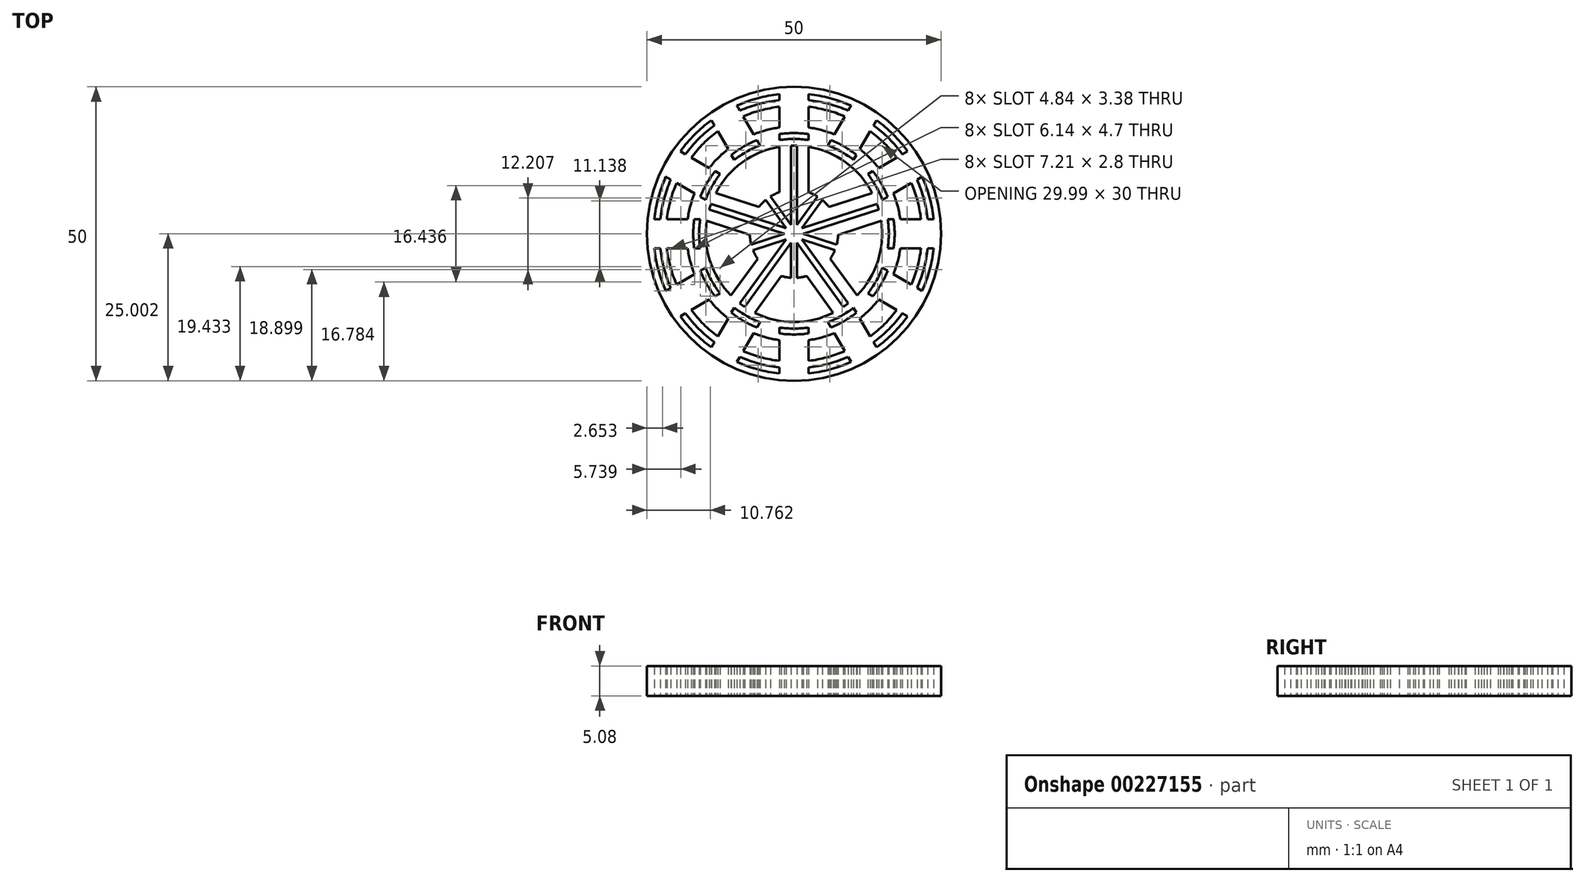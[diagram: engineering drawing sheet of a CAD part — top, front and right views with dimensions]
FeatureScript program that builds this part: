
annotation { "Feature Type Name" : "Feature", "Feature Type Description" : "" }
export const myFeature = defineFeature(function(context is Context, id is Id, definition is map)
    precondition{}
    {
        {
            var Q0;
            Q0=qCreatedBy(makeId("Top.planeOp"),FACE);
            var sketch = newSketch(context, id + "F0", { "sketchPlane" : qUnion([Q0])});
            skCircle(sketch, "E0", {"center": v(-126.34, 15.65) * mm, "radius": 25 * mm});
            skCircle(sketch, "E1", {"center": v(-126.34, 15.65) * mm, "radius": 15 * mm});
            skCircle(sketch, "E2", {"center": v(-126.34, 15.65) * mm, "radius": 18.25 * mm});
            skCircle(sketch, "E3", {"center": v(-126.34, 15.65) * mm, "radius": 21.75 * mm});
            skLineSegment(sketch, "E4", {"start": v(-126.34, 40.65) * mm, "end": v(-126.34, -9.35) * mm});
            skLineSegment(sketch, "E5", {"start": v(-128.84, 33.73) * mm, "end": v(-128.84, 37.26) * mm});
            skLineSegment(sketch, "E6.MirrorCS", {"start": v(-123.84, 33.73) * mm, "end": v(-123.84, 37.26) * mm});
            skLineSegment(sketch, "E7.1.0", {"start": v(-133.22, 32.56) * mm, "end": v(-134.98, 35.61) * mm});
            skLineSegment(sketch, "E7.1.1", {"start": v(-137.55, 30.06) * mm, "end": v(-139.31, 33.11) * mm});
            skLineSegment(sketch, "E7.2.0", {"start": v(-140.75, 26.86) * mm, "end": v(-143.8, 28.62) * mm});
            skLineSegment(sketch, "E7.2.1", {"start": v(-143.25, 22.53) * mm, "end": v(-146.3, 24.3) * mm});
            skLineSegment(sketch, "E7.3.0", {"start": v(-144.42, 18.15) * mm, "end": v(-147.95, 18.15) * mm});
            skLineSegment(sketch, "E7.3.1", {"start": v(-144.42, 13.15) * mm, "end": v(-147.95, 13.15) * mm});
            skLineSegment(sketch, "E7.4.0", {"start": v(-143.25, 8.78) * mm, "end": v(-146.3, 7.01) * mm});
            skLineSegment(sketch, "E7.4.1", {"start": v(-140.75, 4.45) * mm, "end": v(-143.8, 2.68) * mm});
            skLineSegment(sketch, "E7.5.0", {"start": v(-137.55, 1.25) * mm, "end": v(-139.31, -1.8) * mm});
            skLineSegment(sketch, "E7.5.1", {"start": v(-133.22, -1.25) * mm, "end": v(-134.98, -4.3) * mm});
            skLineSegment(sketch, "E7.6.0", {"start": v(-128.84, -2.43) * mm, "end": v(-128.84, -5.95) * mm});
            skLineSegment(sketch, "E7.6.1", {"start": v(-123.84, -2.43) * mm, "end": v(-123.84, -5.95) * mm});
            skLineSegment(sketch, "E7.7.0", {"start": v(-119.47, -1.25) * mm, "end": v(-117.7, -4.3) * mm});
            skLineSegment(sketch, "E7.7.1", {"start": v(-115.14, 1.25) * mm, "end": v(-113.38, -1.8) * mm});
            skLineSegment(sketch, "E7.8.0", {"start": v(-111.94, 4.45) * mm, "end": v(-108.88, 2.68) * mm});
            skLineSegment(sketch, "E7.8.1", {"start": v(-109.44, 8.78) * mm, "end": v(-106.38, 7.01) * mm});
            skLineSegment(sketch, "E7.9.0", {"start": v(-108.27, 13.15) * mm, "end": v(-104.74, 13.15) * mm});
            skLineSegment(sketch, "E7.9.1", {"start": v(-108.27, 18.15) * mm, "end": v(-104.74, 18.15) * mm});
            skLineSegment(sketch, "E7.10.0", {"start": v(-109.44, 22.53) * mm, "end": v(-106.38, 24.3) * mm});
            skLineSegment(sketch, "E7.10.1", {"start": v(-111.94, 26.86) * mm, "end": v(-108.88, 28.62) * mm});
            skLineSegment(sketch, "E7.11.0", {"start": v(-115.14, 30.06) * mm, "end": v(-113.38, 33.11) * mm});
            skLineSegment(sketch, "E7.11.1", {"start": v(-119.47, 32.56) * mm, "end": v(-117.7, 35.61) * mm});
            skLineSegment(sketch, "E8", {"start": v(-128.84, 33.73) * mm, "end": v(-128.84, 30.44) * mm});
            skLineSegment(sketch, "E9", {"start": v(-133.22, 32.56) * mm, "end": v(-131.57, 29.71) * mm});
            skLineSegment(sketch, "E10.1.0", {"start": v(-140.75, 26.86) * mm, "end": v(-137.9, 25.21) * mm});
            skLineSegment(sketch, "E10.1.1", {"start": v(-137.55, 30.06) * mm, "end": v(-135.9, 27.21) * mm});
            skLineSegment(sketch, "E10.2.0", {"start": v(-144.42, 18.15) * mm, "end": v(-141.13, 18.15) * mm});
            skLineSegment(sketch, "E10.2.1", {"start": v(-143.25, 22.53) * mm, "end": v(-140.4, 20.88) * mm});
            skLineSegment(sketch, "E10.3.0", {"start": v(-143.25, 8.78) * mm, "end": v(-140.4, 10.42) * mm});
            skLineSegment(sketch, "E10.3.1", {"start": v(-144.42, 13.15) * mm, "end": v(-141.13, 13.15) * mm});
            skLineSegment(sketch, "E10.4.0", {"start": v(-137.55, 1.25) * mm, "end": v(-135.9, 4.1) * mm});
            skLineSegment(sketch, "E10.4.1", {"start": v(-140.75, 4.45) * mm, "end": v(-137.9, 6.1) * mm});
            skLineSegment(sketch, "E10.5.0", {"start": v(-128.84, -2.43) * mm, "end": v(-128.84, 0.86) * mm});
            skLineSegment(sketch, "E10.5.1", {"start": v(-133.22, -1.25) * mm, "end": v(-131.57, 1.6) * mm});
            skLineSegment(sketch, "E10.6.0", {"start": v(-119.47, -1.25) * mm, "end": v(-121.11, 1.6) * mm});
            skLineSegment(sketch, "E10.6.1", {"start": v(-123.84, -2.43) * mm, "end": v(-123.84, 0.86) * mm});
            skLineSegment(sketch, "E10.7.0", {"start": v(-111.94, 4.45) * mm, "end": v(-114.79, 6.1) * mm});
            skLineSegment(sketch, "E10.7.1", {"start": v(-115.14, 1.25) * mm, "end": v(-116.78, 4.1) * mm});
            skLineSegment(sketch, "E10.8.0", {"start": v(-108.27, 13.15) * mm, "end": v(-111.55, 13.15) * mm});
            skLineSegment(sketch, "E10.8.1", {"start": v(-109.44, 8.78) * mm, "end": v(-112.29, 10.42) * mm});
            skLineSegment(sketch, "E10.9.0", {"start": v(-109.44, 22.53) * mm, "end": v(-112.29, 20.88) * mm});
            skLineSegment(sketch, "E10.9.1", {"start": v(-108.27, 18.15) * mm, "end": v(-111.55, 18.15) * mm});
            skLineSegment(sketch, "E10.10.0", {"start": v(-115.14, 30.06) * mm, "end": v(-116.78, 27.21) * mm});
            skLineSegment(sketch, "E10.10.1", {"start": v(-111.94, 26.86) * mm, "end": v(-114.79, 25.21) * mm});
            skLineSegment(sketch, "E10.11.0", {"start": v(-123.84, 33.73) * mm, "end": v(-123.84, 30.44) * mm});
            skLineSegment(sketch, "E10.11.1", {"start": v(-119.47, 32.56) * mm, "end": v(-121.11, 29.71) * mm});
            skCircle(sketch, "E11", {"center": v(-126.34, 15.65) * mm, "radius": 7.5 * mm});
            skLineSegment(sketch, "E12", {"start": v(-128.84, 30.44) * mm, "end": v(-128.84, 22.72) * mm});
            skLineSegment(sketch, "E13", {"start": v(-123.84, 30.44) * mm, "end": v(-123.84, 22.72) * mm});
            skLineSegment(sketch, "E14.1.0", {"start": v(-139.64, 22.6) * mm, "end": v(-132.3, 20.21) * mm});
            skLineSegment(sketch, "E14.1.1", {"start": v(-141.18, 17.85) * mm, "end": v(-133.84, 15.46) * mm});
            skLineSegment(sketch, "E14.2.0", {"start": v(-137.06, 5.16) * mm, "end": v(-132.52, 11.4) * mm});
            skLineSegment(sketch, "E14.2.1", {"start": v(-133.02, 2.22) * mm, "end": v(-128.48, 8.46) * mm});
            skLineSegment(sketch, "E14.3.0", {"start": v(-119.67, 2.22) * mm, "end": v(-124.21, 8.46) * mm});
            skLineSegment(sketch, "E14.3.1", {"start": v(-115.63, 5.16) * mm, "end": v(-120.17, 11.4) * mm});
            skLineSegment(sketch, "E14.4.0", {"start": v(-111.5, 17.85) * mm, "end": v(-118.85, 15.46) * mm});
            skLineSegment(sketch, "E14.4.1", {"start": v(-113.05, 22.6) * mm, "end": v(-120.4, 20.21) * mm});
            skLineSegment(sketch, "E15", {"start": v(-126.84, 23.14) * mm, "end": v(-126.84, 30.64) * mm});
            skLineSegment(sketch, "E16.MirrorCS", {"start": v(-125.84, 23.14) * mm, "end": v(-125.84, 30.64) * mm});
            skLineSegment(sketch, "E17", {"start": v(-126.84, 23.14) * mm, "end": v(-126.84, 8.17) * mm});
            skLineSegment(sketch, "E18", {"start": v(-125.84, 23.14) * mm, "end": v(-125.84, 8.17) * mm});
            skLineSegment(sketch, "E19.1.0", {"start": v(-133.3, 18.44) * mm, "end": v(-140.45, 20.76) * mm});
            skLineSegment(sketch, "E19.1.1", {"start": v(-133.62, 17.49) * mm, "end": v(-140.76, 19.8) * mm});
            skLineSegment(sketch, "E19.1.2", {"start": v(-133.3, 18.44) * mm, "end": v(-119.07, 13.82) * mm});
            skLineSegment(sketch, "E19.1.3", {"start": v(-133.62, 17.49) * mm, "end": v(-119.38, 12.86) * mm});
            skLineSegment(sketch, "E19.2.0", {"start": v(-131.15, 9.9) * mm, "end": v(-135.56, 3.82) * mm});
            skLineSegment(sketch, "E19.2.1", {"start": v(-130.34, 9.3) * mm, "end": v(-134.75, 3.23) * mm});
            skLineSegment(sketch, "E19.2.2", {"start": v(-131.15, 9.9) * mm, "end": v(-122.35, 22) * mm});
            skLineSegment(sketch, "E19.2.3", {"start": v(-130.34, 9.3) * mm, "end": v(-121.54, 21.41) * mm});
            skLineSegment(sketch, "E19.3.0", {"start": v(-122.35, 9.3) * mm, "end": v(-117.94, 3.23) * mm});
            skLineSegment(sketch, "E19.3.1", {"start": v(-121.54, 9.9) * mm, "end": v(-117.13, 3.82) * mm});
            skLineSegment(sketch, "E19.3.2", {"start": v(-122.35, 9.3) * mm, "end": v(-131.15, 21.41) * mm});
            skLineSegment(sketch, "E19.3.3", {"start": v(-121.54, 9.9) * mm, "end": v(-130.34, 22) * mm});
            skLineSegment(sketch, "E19.4.0", {"start": v(-119.07, 17.49) * mm, "end": v(-111.93, 19.8) * mm});
            skLineSegment(sketch, "E19.4.1", {"start": v(-119.38, 18.44) * mm, "end": v(-112.24, 20.76) * mm});
            skLineSegment(sketch, "E19.4.2", {"start": v(-119.07, 17.49) * mm, "end": v(-133.3, 12.86) * mm});
            skLineSegment(sketch, "E19.4.3", {"start": v(-119.38, 18.44) * mm, "end": v(-133.62, 13.82) * mm});
            skCircle(sketch, "E20", {"center": v(-126.34, 15.65) * mm, "radius": 23.88 * mm});
            skCircle(sketch, "E21", {"center": v(-126.34, 15.65) * mm, "radius": 22.88 * mm});
            skCircle(sketch, "E22", {"center": v(-126.34, 15.65) * mm, "radius": 17.12 * mm});
            skCircle(sketch, "E23", {"center": v(-126.34, 15.65) * mm, "radius": 16.12 * mm});
            skLineSegment(sketch, "E24", {"start": v(-128.84, 38.4) * mm, "end": v(-128.84, 39.4) * mm});
            skLineSegment(sketch, "E25", {"start": v(-123.84, 38.4) * mm, "end": v(-123.84, 39.4) * mm});
            skLineSegment(sketch, "E26.1.0", {"start": v(-135.55, 36.6) * mm, "end": v(-136.05, 37.46) * mm});
            skLineSegment(sketch, "E26.1.1", {"start": v(-139.88, 34.1) * mm, "end": v(-140.38, 34.96) * mm});
            skLineSegment(sketch, "E26.2.0", {"start": v(-144.79, 29.19) * mm, "end": v(-145.66, 29.69) * mm});
            skLineSegment(sketch, "E26.2.1", {"start": v(-147.29, 24.86) * mm, "end": v(-148.16, 25.36) * mm});
            skLineSegment(sketch, "E26.3.0", {"start": v(-149.08, 18.15) * mm, "end": v(-150.09, 18.15) * mm});
            skLineSegment(sketch, "E26.3.1", {"start": v(-149.08, 13.15) * mm, "end": v(-150.09, 13.15) * mm});
            skLineSegment(sketch, "E26.4.0", {"start": v(-147.29, 6.45) * mm, "end": v(-148.16, 5.95) * mm});
            skLineSegment(sketch, "E26.4.1", {"start": v(-144.79, 2.12) * mm, "end": v(-145.66, 1.62) * mm});
            skLineSegment(sketch, "E26.5.0", {"start": v(-139.88, -2.79) * mm, "end": v(-140.38, -3.66) * mm});
            skLineSegment(sketch, "E26.5.1", {"start": v(-135.55, -5.29) * mm, "end": v(-136.05, -6.16) * mm});
            skLineSegment(sketch, "E26.6.0", {"start": v(-128.84, -7.09) * mm, "end": v(-128.84, -8.1) * mm});
            skLineSegment(sketch, "E26.6.1", {"start": v(-123.84, -7.09) * mm, "end": v(-123.84, -8.1) * mm});
            skLineSegment(sketch, "E26.7.0", {"start": v(-117.14, -5.29) * mm, "end": v(-116.64, -6.16) * mm});
            skLineSegment(sketch, "E26.7.1", {"start": v(-112.81, -2.79) * mm, "end": v(-112.3, -3.66) * mm});
            skLineSegment(sketch, "E26.8.0", {"start": v(-107.9, 2.12) * mm, "end": v(-107.03, 1.62) * mm});
            skLineSegment(sketch, "E26.8.1", {"start": v(-105.4, 6.45) * mm, "end": v(-104.53, 5.95) * mm});
            skLineSegment(sketch, "E26.9.0", {"start": v(-103.6, 13.15) * mm, "end": v(-102.6, 13.15) * mm});
            skLineSegment(sketch, "E26.9.1", {"start": v(-103.6, 18.15) * mm, "end": v(-102.6, 18.15) * mm});
            skLineSegment(sketch, "E26.10.0", {"start": v(-105.4, 24.86) * mm, "end": v(-104.53, 25.36) * mm});
            skLineSegment(sketch, "E26.10.1", {"start": v(-107.9, 29.19) * mm, "end": v(-107.03, 29.69) * mm});
            skLineSegment(sketch, "E26.11.0", {"start": v(-112.81, 34.1) * mm, "end": v(-112.3, 34.96) * mm});
            skLineSegment(sketch, "E26.11.1", {"start": v(-117.14, 36.6) * mm, "end": v(-116.64, 37.46) * mm});
            skSolve(sketch);
        }
        {
            var Q0;
            {var subQ0=sQuery(id+"F0.wireOp",EDGE,"E10.7.0");var subQ1=sQuery(id+"F0.wireOp",EDGE,"E1");var subQ2=makeQuery(id+"F0.imprint","INTERSECT",VERTEX,{"derivedFrom":[subQ1,subQ0]});Q0=makeQuery(id+"F0.imprint","IMPRINT",FACE,{"disambiguationData":[TD([[makeQuery(id+"F0.imprint","IMPRINT",EDGE,{"disambiguationData":[TD([[subQ2,-1.0]])],"derivedFrom":subQ1}),-1.0]])]});}
            var Q1;
            {var subQ0=sQuery(id+"F0.wireOp",EDGE,"E10.7.0");var subQ5=sQuery(id+"F0.wireOp",EDGE,"E22");var subQ7=makeQuery(id+"F0.imprint","INTERSECT",VERTEX,{"derivedFrom":[subQ0,subQ5]});Q1=makeQuery(id+"F0.imprint","IMPRINT",FACE,{"disambiguationData":[TD([[makeQuery(id+"F0.imprint","IMPRINT",EDGE,{"disambiguationData":[TD([[subQ7,-1.0]])],"derivedFrom":subQ5}),-1.0]])]});}
            var Q2;
            {var subQ0=sQuery(id+"F0.wireOp",EDGE,"E10.5.0");var subQ1=sQuery(id+"F0.wireOp",EDGE,"E1");var subQ2=makeQuery(id+"F0.imprint","INTERSECT",VERTEX,{"derivedFrom":[subQ1,subQ0]});Q2=makeQuery(id+"F0.imprint","IMPRINT",FACE,{"disambiguationData":[TD([[makeQuery(id+"F0.imprint","IMPRINT",EDGE,{"disambiguationData":[TD([[subQ2,-1.0]])],"derivedFrom":subQ1}),-1.0]])]});}
            var Q3;
            {var subQ1=sQuery(id+"F0.wireOp",EDGE,"E2");var subQ3=sQuery(id+"F0.wireOp",EDGE,"E4");var subQ4=makeQuery(id+"F0.imprint","INTERSECT",VERTEX,{"disambiguationData":[OD(1.0)],"derivedFrom":[subQ1,subQ3]});Q3=makeQuery(id+"F0.imprint","IMPRINT",FACE,{"disambiguationData":[TD([[makeQuery(id+"F0.imprint","IMPRINT",EDGE,{"disambiguationData":[TD([[subQ4,1.0]])],"derivedFrom":subQ3}),-1.0]])]});}
            var Q4;
            {var subQ0=sQuery(id+"F0.wireOp",EDGE,"E5");Q4=makeQuery(id+"F0.imprint","IMPRINT",FACE,{"disambiguationData":[TD([[makeQuery(id+"F0.imprint","IMPRINT",EDGE,{"derivedFrom":subQ0}),-1.0]])]});}
            var Q5;
            {var subQ0=sQuery(id+"F0.wireOp",EDGE,"E7.6.0");Q5=makeQuery(id+"F0.imprint","IMPRINT",FACE,{"disambiguationData":[TD([[makeQuery(id+"F0.imprint","IMPRINT",EDGE,{"derivedFrom":subQ0}),1.0]])]});}
            var Q6;
            {var subQ0=sQuery(id+"F0.wireOp",EDGE,"E4");var subQ1=sQuery(id+"F0.wireOp",EDGE,"E0");var subQ2=makeQuery(id+"F0.imprint","INTERSECT",VERTEX,{"disambiguationData":[OD(0.0)],"derivedFrom":[subQ1,subQ0]});Q6=makeQuery(id+"F0.imprint","IMPRINT",FACE,{"disambiguationData":[TD([[makeQuery(id+"F0.imprint","IMPRINT",EDGE,{"disambiguationData":[TD([[subQ2,-1.0]])],"derivedFrom":subQ1}),1.0]])]});}
            var Q7;
            {var subQ0=sQuery(id+"F0.wireOp",EDGE,"E4");var subQ1=sQuery(id+"F0.wireOp",EDGE,"E0");var subQ2=makeQuery(id+"F0.imprint","INTERSECT",VERTEX,{"disambiguationData":[OD(0.0)],"derivedFrom":[subQ1,subQ0]});Q7=makeQuery(id+"F0.imprint","IMPRINT",FACE,{"disambiguationData":[TD([[makeQuery(id+"F0.imprint","IMPRINT",EDGE,{"disambiguationData":[TD([[subQ2,1.0]])],"derivedFrom":subQ1}),1.0]])]});}
            var Q8;
            {var subQ0=sQuery(id+"F0.wireOp",EDGE,"E9");var subQ1=sQuery(id+"F0.wireOp",EDGE,"E1");var subQ2=makeQuery(id+"F0.imprint","INTERSECT",VERTEX,{"derivedFrom":[subQ1,subQ0]});Q8=makeQuery(id+"F0.imprint","IMPRINT",FACE,{"disambiguationData":[TD([[makeQuery(id+"F0.imprint","IMPRINT",EDGE,{"disambiguationData":[TD([[subQ2,-1.0]])],"derivedFrom":subQ1}),-1.0]])]});}
            var Q9;
            {var subQ0=sQuery(id+"F0.wireOp",EDGE,"E9");var subQ5=sQuery(id+"F0.wireOp",EDGE,"E22");var subQ6=makeQuery(id+"F0.imprint","INTERSECT",VERTEX,{"derivedFrom":[subQ0,subQ5]});Q9=makeQuery(id+"F0.imprint","IMPRINT",FACE,{"disambiguationData":[TD([[makeQuery(id+"F0.imprint","IMPRINT",EDGE,{"disambiguationData":[TD([[subQ6,-1.0]])],"derivedFrom":subQ5}),-1.0]])]});}
            var Q10;
            {var subQ0=sQuery(id+"F0.wireOp",EDGE,"E7.1.0");Q10=makeQuery(id+"F0.imprint","IMPRINT",FACE,{"disambiguationData":[TD([[makeQuery(id+"F0.imprint","IMPRINT",EDGE,{"derivedFrom":subQ0}),1.0]])]});}
            var Q11;
            {var subQ0=sQuery(id+"F0.wireOp",EDGE,"E7.2.0");Q11=makeQuery(id+"F0.imprint","IMPRINT",FACE,{"disambiguationData":[TD([[makeQuery(id+"F0.imprint","IMPRINT",EDGE,{"derivedFrom":subQ0}),1.0]])]});}
            var Q12;
            {var subQ0=sQuery(id+"F0.wireOp",EDGE,"E10.1.0");var subQ5=sQuery(id+"F0.wireOp",EDGE,"E22");var subQ6=makeQuery(id+"F0.imprint","INTERSECT",VERTEX,{"derivedFrom":[subQ0,subQ5]});Q12=makeQuery(id+"F0.imprint","IMPRINT",FACE,{"disambiguationData":[TD([[makeQuery(id+"F0.imprint","IMPRINT",EDGE,{"disambiguationData":[TD([[subQ6,-1.0]])],"derivedFrom":subQ5}),-1.0]])]});}
            var Q13;
            {var subQ0=sQuery(id+"F0.wireOp",EDGE,"E7.3.0");Q13=makeQuery(id+"F0.imprint","IMPRINT",FACE,{"disambiguationData":[TD([[makeQuery(id+"F0.imprint","IMPRINT",EDGE,{"derivedFrom":subQ0}),1.0]])]});}
            var Q14;
            {var subQ0=sQuery(id+"F0.wireOp",EDGE,"E10.2.0");var subQ5=sQuery(id+"F0.wireOp",EDGE,"E22");var subQ6=makeQuery(id+"F0.imprint","INTERSECT",VERTEX,{"derivedFrom":[subQ0,subQ5]});Q14=makeQuery(id+"F0.imprint","IMPRINT",FACE,{"disambiguationData":[TD([[makeQuery(id+"F0.imprint","IMPRINT",EDGE,{"disambiguationData":[TD([[subQ6,-1.0]])],"derivedFrom":subQ5}),-1.0]])]});}
            var Q15;
            {var subQ0=sQuery(id+"F0.wireOp",EDGE,"E10.1.0");var subQ1=sQuery(id+"F0.wireOp",EDGE,"E1");var subQ2=makeQuery(id+"F0.imprint","INTERSECT",VERTEX,{"derivedFrom":[subQ1,subQ0]});Q15=makeQuery(id+"F0.imprint","IMPRINT",FACE,{"disambiguationData":[TD([[makeQuery(id+"F0.imprint","IMPRINT",EDGE,{"disambiguationData":[TD([[subQ2,1.0]])],"derivedFrom":subQ1}),-1.0]])]});}
            var Q16;
            {var subQ3=sQuery(id+"F0.wireOp",EDGE,"E10.1.0");var subQ5=sQuery(id+"F0.wireOp",EDGE,"E22");var subQ6=makeQuery(id+"F0.imprint","INTERSECT",VERTEX,{"derivedFrom":[subQ3,subQ5]});Q16=makeQuery(id+"F0.imprint","IMPRINT",FACE,{"disambiguationData":[TD([[makeQuery(id+"F0.imprint","IMPRINT",EDGE,{"disambiguationData":[TD([[subQ6,1.0]])],"derivedFrom":subQ5}),-1.0]])]});}
            var Q17;
            {var subQ3=sQuery(id+"F0.wireOp",EDGE,"E10.2.0");var subQ5=sQuery(id+"F0.wireOp",EDGE,"E22");var subQ6=makeQuery(id+"F0.imprint","INTERSECT",VERTEX,{"derivedFrom":[subQ3,subQ5]});Q17=makeQuery(id+"F0.imprint","IMPRINT",FACE,{"disambiguationData":[TD([[makeQuery(id+"F0.imprint","IMPRINT",EDGE,{"disambiguationData":[TD([[subQ6,1.0]])],"derivedFrom":subQ5}),-1.0]])]});}
            var Q18;
            {var subQ0=sQuery(id+"F0.wireOp",EDGE,"E10.3.0");var subQ1=sQuery(id+"F0.wireOp",EDGE,"E1");var subQ2=makeQuery(id+"F0.imprint","INTERSECT",VERTEX,{"derivedFrom":[subQ1,subQ0]});Q18=makeQuery(id+"F0.imprint","IMPRINT",FACE,{"disambiguationData":[TD([[makeQuery(id+"F0.imprint","IMPRINT",EDGE,{"disambiguationData":[TD([[subQ2,1.0]])],"derivedFrom":subQ1}),-1.0]])]});}
            var Q19;
            {var subQ3=sQuery(id+"F0.wireOp",EDGE,"E10.3.0");var subQ5=sQuery(id+"F0.wireOp",EDGE,"E22");var subQ7=makeQuery(id+"F0.imprint","INTERSECT",VERTEX,{"derivedFrom":[subQ3,subQ5]});Q19=makeQuery(id+"F0.imprint","IMPRINT",FACE,{"disambiguationData":[TD([[makeQuery(id+"F0.imprint","IMPRINT",EDGE,{"disambiguationData":[TD([[subQ7,1.0]])],"derivedFrom":subQ5}),-1.0]])]});}
            var Q20;
            {var subQ0=sQuery(id+"F0.wireOp",EDGE,"E10.3.0");var subQ1=sQuery(id+"F0.wireOp",EDGE,"E1");var subQ2=makeQuery(id+"F0.imprint","INTERSECT",VERTEX,{"derivedFrom":[subQ1,subQ0]});Q20=makeQuery(id+"F0.imprint","IMPRINT",FACE,{"disambiguationData":[TD([[makeQuery(id+"F0.imprint","IMPRINT",EDGE,{"disambiguationData":[TD([[subQ2,-1.0]])],"derivedFrom":subQ1}),-1.0]])]});}
            var Q21;
            {var subQ0=sQuery(id+"F0.wireOp",EDGE,"E10.3.0");var subQ5=sQuery(id+"F0.wireOp",EDGE,"E22");var subQ7=makeQuery(id+"F0.imprint","INTERSECT",VERTEX,{"derivedFrom":[subQ0,subQ5]});Q21=makeQuery(id+"F0.imprint","IMPRINT",FACE,{"disambiguationData":[TD([[makeQuery(id+"F0.imprint","IMPRINT",EDGE,{"disambiguationData":[TD([[subQ7,-1.0]])],"derivedFrom":subQ5}),-1.0]])]});}
            var Q22;
            {var subQ0=sQuery(id+"F0.wireOp",EDGE,"E7.4.0");Q22=makeQuery(id+"F0.imprint","IMPRINT",FACE,{"disambiguationData":[TD([[makeQuery(id+"F0.imprint","IMPRINT",EDGE,{"derivedFrom":subQ0}),1.0]])]});}
            var Q23;
            {var subQ0=sQuery(id+"F0.wireOp",EDGE,"E7.5.0");Q23=makeQuery(id+"F0.imprint","IMPRINT",FACE,{"disambiguationData":[TD([[makeQuery(id+"F0.imprint","IMPRINT",EDGE,{"derivedFrom":subQ0}),1.0]])]});}
            var Q24;
            {var subQ0=sQuery(id+"F0.wireOp",EDGE,"E10.4.0");var subQ5=sQuery(id+"F0.wireOp",EDGE,"E22");var subQ6=makeQuery(id+"F0.imprint","INTERSECT",VERTEX,{"derivedFrom":[subQ0,subQ5]});Q24=makeQuery(id+"F0.imprint","IMPRINT",FACE,{"disambiguationData":[TD([[makeQuery(id+"F0.imprint","IMPRINT",EDGE,{"disambiguationData":[TD([[subQ6,-1.0]])],"derivedFrom":subQ5}),-1.0]])]});}
            var Q25;
            {var subQ3=sQuery(id+"F0.wireOp",EDGE,"E10.4.0");var subQ5=sQuery(id+"F0.wireOp",EDGE,"E22");var subQ6=makeQuery(id+"F0.imprint","INTERSECT",VERTEX,{"derivedFrom":[subQ3,subQ5]});Q25=makeQuery(id+"F0.imprint","IMPRINT",FACE,{"disambiguationData":[TD([[makeQuery(id+"F0.imprint","IMPRINT",EDGE,{"disambiguationData":[TD([[subQ6,1.0]])],"derivedFrom":subQ5}),-1.0]])]});}
            var Q26;
            {var subQ0=sQuery(id+"F0.wireOp",EDGE,"E10.5.0");var subQ1=sQuery(id+"F0.wireOp",EDGE,"E1");var subQ2=makeQuery(id+"F0.imprint","INTERSECT",VERTEX,{"derivedFrom":[subQ1,subQ0]});Q26=makeQuery(id+"F0.imprint","IMPRINT",FACE,{"disambiguationData":[TD([[makeQuery(id+"F0.imprint","IMPRINT",EDGE,{"disambiguationData":[TD([[subQ2,1.0]])],"derivedFrom":subQ1}),-1.0]])]});}
            var Q27;
            {var subQ3=sQuery(id+"F0.wireOp",EDGE,"E10.5.0");var subQ5=sQuery(id+"F0.wireOp",EDGE,"E22");var subQ6=makeQuery(id+"F0.imprint","INTERSECT",VERTEX,{"derivedFrom":[subQ3,subQ5]});Q27=makeQuery(id+"F0.imprint","IMPRINT",FACE,{"disambiguationData":[TD([[makeQuery(id+"F0.imprint","IMPRINT",EDGE,{"disambiguationData":[TD([[subQ6,1.0]])],"derivedFrom":subQ5}),-1.0]])]});}
            var Q28;
            {var subQ0=sQuery(id+"F0.wireOp",EDGE,"E10.6.1");var subQ1=sQuery(id+"F0.wireOp",EDGE,"E1");var subQ2=makeQuery(id+"F0.imprint","INTERSECT",VERTEX,{"derivedFrom":[subQ1,subQ0]});Q28=makeQuery(id+"F0.imprint","IMPRINT",FACE,{"disambiguationData":[TD([[makeQuery(id+"F0.imprint","IMPRINT",EDGE,{"disambiguationData":[TD([[subQ2,1.0]])],"derivedFrom":subQ1}),-1.0]])]});}
            var Q29;
            {var subQ1=sQuery(id+"F0.wireOp",EDGE,"E2");var subQ3=sQuery(id+"F0.wireOp",EDGE,"E4");var subQ4=makeQuery(id+"F0.imprint","INTERSECT",VERTEX,{"disambiguationData":[OD(1.0)],"derivedFrom":[subQ1,subQ3]});Q29=makeQuery(id+"F0.imprint","IMPRINT",FACE,{"disambiguationData":[TD([[makeQuery(id+"F0.imprint","IMPRINT",EDGE,{"disambiguationData":[TD([[subQ4,1.0]])],"derivedFrom":subQ3}),1.0]])]});}
            var Q30;
            {var subQ0=sQuery(id+"F0.wireOp",EDGE,"E7.6.1");Q30=makeQuery(id+"F0.imprint","IMPRINT",FACE,{"disambiguationData":[TD([[makeQuery(id+"F0.imprint","IMPRINT",EDGE,{"derivedFrom":subQ0}),-1.0]])]});}
            var Q31;
            {var subQ0=sQuery(id+"F0.wireOp",EDGE,"E10.6.0");var subQ1=sQuery(id+"F0.wireOp",EDGE,"E1");var subQ2=makeQuery(id+"F0.imprint","INTERSECT",VERTEX,{"derivedFrom":[subQ1,subQ0]});Q31=makeQuery(id+"F0.imprint","IMPRINT",FACE,{"disambiguationData":[TD([[makeQuery(id+"F0.imprint","IMPRINT",EDGE,{"disambiguationData":[TD([[subQ2,1.0]])],"derivedFrom":subQ1}),-1.0]])]});}
            var Q32;
            {var subQ3=sQuery(id+"F0.wireOp",EDGE,"E10.6.0");var subQ5=sQuery(id+"F0.wireOp",EDGE,"E22");var subQ6=makeQuery(id+"F0.imprint","INTERSECT",VERTEX,{"derivedFrom":[subQ3,subQ5]});Q32=makeQuery(id+"F0.imprint","IMPRINT",FACE,{"disambiguationData":[TD([[makeQuery(id+"F0.imprint","IMPRINT",EDGE,{"disambiguationData":[TD([[subQ6,1.0]])],"derivedFrom":subQ5}),-1.0]])]});}
            var Q33;
            {var subQ0=sQuery(id+"F0.wireOp",EDGE,"E10.6.0");var subQ5=sQuery(id+"F0.wireOp",EDGE,"E22");var subQ6=makeQuery(id+"F0.imprint","INTERSECT",VERTEX,{"derivedFrom":[subQ0,subQ5]});Q33=makeQuery(id+"F0.imprint","IMPRINT",FACE,{"disambiguationData":[TD([[makeQuery(id+"F0.imprint","IMPRINT",EDGE,{"disambiguationData":[TD([[subQ6,-1.0]])],"derivedFrom":subQ5}),-1.0]])]});}
            var Q34;
            {var subQ3=sQuery(id+"F0.wireOp",EDGE,"E10.7.0");var subQ5=sQuery(id+"F0.wireOp",EDGE,"E22");var subQ7=makeQuery(id+"F0.imprint","INTERSECT",VERTEX,{"derivedFrom":[subQ3,subQ5]});Q34=makeQuery(id+"F0.imprint","IMPRINT",FACE,{"disambiguationData":[TD([[makeQuery(id+"F0.imprint","IMPRINT",EDGE,{"disambiguationData":[TD([[subQ7,1.0]])],"derivedFrom":subQ5}),-1.0]])]});}
            var Q35;
            {var subQ0=sQuery(id+"F0.wireOp",EDGE,"E10.8.0");var subQ1=sQuery(id+"F0.wireOp",EDGE,"E1");var subQ2=makeQuery(id+"F0.imprint","INTERSECT",VERTEX,{"derivedFrom":[subQ1,subQ0]});Q35=makeQuery(id+"F0.imprint","IMPRINT",FACE,{"disambiguationData":[TD([[makeQuery(id+"F0.imprint","IMPRINT",EDGE,{"disambiguationData":[TD([[subQ2,1.0]])],"derivedFrom":subQ1}),-1.0]])]});}
            var Q36;
            {var subQ3=sQuery(id+"F0.wireOp",EDGE,"E10.8.0");var subQ5=sQuery(id+"F0.wireOp",EDGE,"E22");var subQ6=makeQuery(id+"F0.imprint","INTERSECT",VERTEX,{"derivedFrom":[subQ3,subQ5]});Q36=makeQuery(id+"F0.imprint","IMPRINT",FACE,{"disambiguationData":[TD([[makeQuery(id+"F0.imprint","IMPRINT",EDGE,{"disambiguationData":[TD([[subQ6,1.0]])],"derivedFrom":subQ5}),-1.0]])]});}
            var Q37;
            {var subQ0=sQuery(id+"F0.wireOp",EDGE,"E10.8.0");var subQ5=sQuery(id+"F0.wireOp",EDGE,"E22");var subQ6=makeQuery(id+"F0.imprint","INTERSECT",VERTEX,{"derivedFrom":[subQ0,subQ5]});Q37=makeQuery(id+"F0.imprint","IMPRINT",FACE,{"disambiguationData":[TD([[makeQuery(id+"F0.imprint","IMPRINT",EDGE,{"disambiguationData":[TD([[subQ6,-1.0]])],"derivedFrom":subQ5}),-1.0]])]});}
            var Q38;
            {var subQ3=sQuery(id+"F0.wireOp",EDGE,"E10.9.0");var subQ5=sQuery(id+"F0.wireOp",EDGE,"E22");var subQ6=makeQuery(id+"F0.imprint","INTERSECT",VERTEX,{"derivedFrom":[subQ3,subQ5]});Q38=makeQuery(id+"F0.imprint","IMPRINT",FACE,{"disambiguationData":[TD([[makeQuery(id+"F0.imprint","IMPRINT",EDGE,{"disambiguationData":[TD([[subQ6,1.0]])],"derivedFrom":subQ5}),-1.0]])]});}
            var Q39;
            {var subQ0=sQuery(id+"F0.wireOp",EDGE,"E10.9.0");var subQ5=sQuery(id+"F0.wireOp",EDGE,"E22");var subQ6=makeQuery(id+"F0.imprint","INTERSECT",VERTEX,{"derivedFrom":[subQ0,subQ5]});Q39=makeQuery(id+"F0.imprint","IMPRINT",FACE,{"disambiguationData":[TD([[makeQuery(id+"F0.imprint","IMPRINT",EDGE,{"disambiguationData":[TD([[subQ6,-1.0]])],"derivedFrom":subQ5}),-1.0]])]});}
            var Q40;
            {var subQ0=sQuery(id+"F0.wireOp",EDGE,"E10.10.0");var subQ1=sQuery(id+"F0.wireOp",EDGE,"E1");var subQ2=makeQuery(id+"F0.imprint","INTERSECT",VERTEX,{"derivedFrom":[subQ1,subQ0]});Q40=makeQuery(id+"F0.imprint","IMPRINT",FACE,{"disambiguationData":[TD([[makeQuery(id+"F0.imprint","IMPRINT",EDGE,{"disambiguationData":[TD([[subQ2,1.0]])],"derivedFrom":subQ1}),-1.0]])]});}
            var Q41;
            {var subQ3=sQuery(id+"F0.wireOp",EDGE,"E10.10.0");var subQ5=sQuery(id+"F0.wireOp",EDGE,"E22");var subQ6=makeQuery(id+"F0.imprint","INTERSECT",VERTEX,{"derivedFrom":[subQ3,subQ5]});Q41=makeQuery(id+"F0.imprint","IMPRINT",FACE,{"disambiguationData":[TD([[makeQuery(id+"F0.imprint","IMPRINT",EDGE,{"disambiguationData":[TD([[subQ6,1.0]])],"derivedFrom":subQ5}),-1.0]])]});}
            var Q42;
            {var subQ0=sQuery(id+"F0.wireOp",EDGE,"E10.10.0");var subQ1=sQuery(id+"F0.wireOp",EDGE,"E1");var subQ2=makeQuery(id+"F0.imprint","INTERSECT",VERTEX,{"derivedFrom":[subQ1,subQ0]});Q42=makeQuery(id+"F0.imprint","IMPRINT",FACE,{"disambiguationData":[TD([[makeQuery(id+"F0.imprint","IMPRINT",EDGE,{"disambiguationData":[TD([[subQ2,-1.0]])],"derivedFrom":subQ1}),-1.0]])]});}
            var Q43;
            {var subQ0=sQuery(id+"F0.wireOp",EDGE,"E10.10.0");var subQ5=sQuery(id+"F0.wireOp",EDGE,"E22");var subQ6=makeQuery(id+"F0.imprint","INTERSECT",VERTEX,{"derivedFrom":[subQ0,subQ5]});Q43=makeQuery(id+"F0.imprint","IMPRINT",FACE,{"disambiguationData":[TD([[makeQuery(id+"F0.imprint","IMPRINT",EDGE,{"disambiguationData":[TD([[subQ6,-1.0]])],"derivedFrom":subQ5}),-1.0]])]});}
            var Q44;
            {var subQ1=sQuery(id+"F0.wireOp",EDGE,"E1");var subQ3=sQuery(id+"F0.wireOp",EDGE,"E10.11.1");var subQ4=makeQuery(id+"F0.imprint","INTERSECT",VERTEX,{"derivedFrom":[subQ1,subQ3]});Q44=makeQuery(id+"F0.imprint","IMPRINT",FACE,{"disambiguationData":[TD([[makeQuery(id+"F0.imprint","IMPRINT",EDGE,{"disambiguationData":[TD([[subQ4,1.0]])],"derivedFrom":subQ3}),-1.0]])]});}
            var Q45;
            {var subQ0=sQuery(id+"F0.wireOp",EDGE,"E10.11.0");var subQ5=sQuery(id+"F0.wireOp",EDGE,"E22");var subQ6=makeQuery(id+"F0.imprint","INTERSECT",VERTEX,{"derivedFrom":[subQ0,subQ5]});Q45=makeQuery(id+"F0.imprint","IMPRINT",FACE,{"disambiguationData":[TD([[makeQuery(id+"F0.imprint","IMPRINT",EDGE,{"disambiguationData":[TD([[subQ6,1.0]])],"derivedFrom":subQ5}),-1.0]])]});}
            var Q46;
            {var subQ1=sQuery(id+"F0.wireOp",EDGE,"E2");var subQ3=sQuery(id+"F0.wireOp",EDGE,"E4");var subQ4=makeQuery(id+"F0.imprint","INTERSECT",VERTEX,{"disambiguationData":[OD(0.0)],"derivedFrom":[subQ1,subQ3]});Q46=makeQuery(id+"F0.imprint","IMPRINT",FACE,{"disambiguationData":[TD([[makeQuery(id+"F0.imprint","IMPRINT",EDGE,{"disambiguationData":[TD([[subQ4,-1.0]])],"derivedFrom":subQ3}),1.0]])]});}
            var Q47;
            {var subQ1=sQuery(id+"F0.wireOp",EDGE,"E2");var subQ3=sQuery(id+"F0.wireOp",EDGE,"E4");var subQ4=makeQuery(id+"F0.imprint","INTERSECT",VERTEX,{"disambiguationData":[OD(0.0)],"derivedFrom":[subQ1,subQ3]});Q47=makeQuery(id+"F0.imprint","IMPRINT",FACE,{"disambiguationData":[TD([[makeQuery(id+"F0.imprint","IMPRINT",EDGE,{"disambiguationData":[TD([[subQ4,-1.0]])],"derivedFrom":subQ3}),-1.0]])]});}
            var Q48;
            {var subQ1=sQuery(id+"F0.wireOp",EDGE,"E1");var subQ3=sQuery(id+"F0.wireOp",EDGE,"E9");var subQ4=makeQuery(id+"F0.imprint","INTERSECT",VERTEX,{"derivedFrom":[subQ1,subQ3]});Q48=makeQuery(id+"F0.imprint","IMPRINT",FACE,{"disambiguationData":[TD([[makeQuery(id+"F0.imprint","IMPRINT",EDGE,{"disambiguationData":[TD([[subQ4,1.0]])],"derivedFrom":subQ3}),1.0]])]});}
            var Q49;
            {var subQ0=sQuery(id+"F0.wireOp",EDGE,"E8");var subQ5=sQuery(id+"F0.wireOp",EDGE,"E22");var subQ6=makeQuery(id+"F0.imprint","INTERSECT",VERTEX,{"derivedFrom":[subQ0,subQ5]});Q49=makeQuery(id+"F0.imprint","IMPRINT",FACE,{"disambiguationData":[TD([[makeQuery(id+"F0.imprint","IMPRINT",EDGE,{"disambiguationData":[TD([[subQ6,-1.0]])],"derivedFrom":subQ5}),-1.0]])]});}
            var Q50;
            {var subQ0=sQuery(id+"F0.wireOp",EDGE,"E6.MirrorCS");Q50=makeQuery(id+"F0.imprint","IMPRINT",FACE,{"disambiguationData":[TD([[makeQuery(id+"F0.imprint","IMPRINT",EDGE,{"derivedFrom":subQ0}),1.0]])]});}
            var Q51;
            {var subQ0=sQuery(id+"F0.wireOp",EDGE,"E7.11.0");Q51=makeQuery(id+"F0.imprint","IMPRINT",FACE,{"disambiguationData":[TD([[makeQuery(id+"F0.imprint","IMPRINT",EDGE,{"derivedFrom":subQ0}),1.0]])]});}
            var Q52;
            {var subQ0=sQuery(id+"F0.wireOp",EDGE,"E7.10.0");Q52=makeQuery(id+"F0.imprint","IMPRINT",FACE,{"disambiguationData":[TD([[makeQuery(id+"F0.imprint","IMPRINT",EDGE,{"derivedFrom":subQ0}),1.0]])]});}
            var Q53;
            {var subQ0=sQuery(id+"F0.wireOp",EDGE,"E7.9.0");Q53=makeQuery(id+"F0.imprint","IMPRINT",FACE,{"disambiguationData":[TD([[makeQuery(id+"F0.imprint","IMPRINT",EDGE,{"derivedFrom":subQ0}),1.0]])]});}
            var Q54;
            {var subQ0=sQuery(id+"F0.wireOp",EDGE,"E7.8.0");Q54=makeQuery(id+"F0.imprint","IMPRINT",FACE,{"disambiguationData":[TD([[makeQuery(id+"F0.imprint","IMPRINT",EDGE,{"derivedFrom":subQ0}),1.0]])]});}
            var Q55;
            {var subQ0=sQuery(id+"F0.wireOp",EDGE,"E7.7.0");Q55=makeQuery(id+"F0.imprint","IMPRINT",FACE,{"disambiguationData":[TD([[makeQuery(id+"F0.imprint","IMPRINT",EDGE,{"derivedFrom":subQ0}),1.0]])]});}
            var Q56;
            {var subQ0=sQuery(id+"F0.wireOp",EDGE,"E14.1.0");Q56=makeQuery(id+"F0.imprint","IMPRINT",FACE,{"disambiguationData":[TD([[makeQuery(id+"F0.imprint","IMPRINT",EDGE,{"derivedFrom":subQ0}),-1.0]])]});}
            var Q57;
            {var subQ0=sQuery(id+"F0.wireOp",EDGE,"E13");Q57=makeQuery(id+"F0.imprint","IMPRINT",FACE,{"disambiguationData":[TD([[makeQuery(id+"F0.imprint","IMPRINT",EDGE,{"derivedFrom":subQ0}),-1.0]])]});}
            var Q58;
            {var subQ0=sQuery(id+"F0.wireOp",EDGE,"E12");Q58=makeQuery(id+"F0.imprint","IMPRINT",FACE,{"disambiguationData":[TD([[makeQuery(id+"F0.imprint","IMPRINT",EDGE,{"derivedFrom":subQ0}),1.0]])]});}
            var Q59;
            {var subQ0=sQuery(id+"F0.wireOp",EDGE,"E14.4.0");Q59=makeQuery(id+"F0.imprint","IMPRINT",FACE,{"disambiguationData":[TD([[makeQuery(id+"F0.imprint","IMPRINT",EDGE,{"derivedFrom":subQ0}),-1.0]])]});}
            var Q60;
            {var subQ0=sQuery(id+"F0.wireOp",EDGE,"E14.3.0");Q60=makeQuery(id+"F0.imprint","IMPRINT",FACE,{"disambiguationData":[TD([[makeQuery(id+"F0.imprint","IMPRINT",EDGE,{"derivedFrom":subQ0}),-1.0]])]});}
            var Q61;
            {var subQ0=sQuery(id+"F0.wireOp",EDGE,"E14.2.0");Q61=makeQuery(id+"F0.imprint","IMPRINT",FACE,{"disambiguationData":[TD([[makeQuery(id+"F0.imprint","IMPRINT",EDGE,{"derivedFrom":subQ0}),-1.0]])]});}
            var Q62;
            {var subQ0=sQuery(id+"F0.wireOp",EDGE,"E11");var subQ1=makeQuery(id+"F0.imprint","INTERSECT",VERTEX,{"derivedFrom":[subQ0,sQuery(id+"F0.wireOp",EDGE,"E13")]});Q62=makeQuery(id+"F0.imprint","IMPRINT",FACE,{"disambiguationData":[TD([[makeQuery(id+"F0.imprint","IMPRINT",EDGE,{"disambiguationData":[TD([[subQ1,1.0]])],"derivedFrom":subQ0}),1.0]])]});}
            var Q63;
            {var subQ0=sQuery(id+"F0.wireOp",EDGE,"E11");var subQ1=makeQuery(id+"F0.imprint","INTERSECT",VERTEX,{"derivedFrom":[subQ0,sQuery(id+"F0.wireOp",EDGE,"E12")]});Q63=makeQuery(id+"F0.imprint","IMPRINT",FACE,{"disambiguationData":[TD([[makeQuery(id+"F0.imprint","IMPRINT",EDGE,{"disambiguationData":[TD([[subQ1,-1.0]])],"derivedFrom":subQ0}),1.0]])]});}
            var Q64;
            {var subQ0=sQuery(id+"F0.wireOp",EDGE,"E11");var subQ1=makeQuery(id+"F0.imprint","INTERSECT",VERTEX,{"derivedFrom":[subQ0,sQuery(id+"F0.wireOp",EDGE,"E14.1.0")]});Q64=makeQuery(id+"F0.imprint","IMPRINT",FACE,{"disambiguationData":[TD([[makeQuery(id+"F0.imprint","IMPRINT",EDGE,{"disambiguationData":[TD([[subQ1,1.0]])],"derivedFrom":subQ0}),1.0]])]});}
            var Q65;
            {var subQ0=sQuery(id+"F0.wireOp",EDGE,"E11");var subQ1=makeQuery(id+"F0.imprint","INTERSECT",VERTEX,{"derivedFrom":[subQ0,sQuery(id+"F0.wireOp",EDGE,"E14.1.1")]});Q65=makeQuery(id+"F0.imprint","IMPRINT",FACE,{"disambiguationData":[TD([[makeQuery(id+"F0.imprint","IMPRINT",EDGE,{"disambiguationData":[TD([[subQ1,-1.0]])],"derivedFrom":subQ0}),1.0]])]});}
            var Q66;
            {var subQ0=sQuery(id+"F0.wireOp",EDGE,"E14.1.1");Q66=makeQuery(id+"F0.imprint","IMPRINT",FACE,{"disambiguationData":[TD([[makeQuery(id+"F0.imprint","IMPRINT",EDGE,{"derivedFrom":subQ0}),1.0]])]});}
            var Q67;
            {var subQ0=sQuery(id+"F0.wireOp",EDGE,"E11");var subQ1=makeQuery(id+"F0.imprint","INTERSECT",VERTEX,{"derivedFrom":[subQ0,sQuery(id+"F0.wireOp",EDGE,"E14.2.0")]});Q67=makeQuery(id+"F0.imprint","IMPRINT",FACE,{"disambiguationData":[TD([[makeQuery(id+"F0.imprint","IMPRINT",EDGE,{"disambiguationData":[TD([[subQ1,1.0]])],"derivedFrom":subQ0}),1.0]])]});}
            var Q68;
            {var subQ0=sQuery(id+"F0.wireOp",EDGE,"E11");var subQ1=makeQuery(id+"F0.imprint","INTERSECT",VERTEX,{"derivedFrom":[subQ0,sQuery(id+"F0.wireOp",EDGE,"E14.2.1")]});Q68=makeQuery(id+"F0.imprint","IMPRINT",FACE,{"disambiguationData":[TD([[makeQuery(id+"F0.imprint","IMPRINT",EDGE,{"disambiguationData":[TD([[subQ1,-1.0]])],"derivedFrom":subQ0}),1.0]])]});}
            var Q69;
            {var subQ0=sQuery(id+"F0.wireOp",EDGE,"E14.2.1");Q69=makeQuery(id+"F0.imprint","IMPRINT",FACE,{"disambiguationData":[TD([[makeQuery(id+"F0.imprint","IMPRINT",EDGE,{"derivedFrom":subQ0}),1.0]])]});}
            var Q70;
            {var subQ0=sQuery(id+"F0.wireOp",EDGE,"E11");var subQ1=makeQuery(id+"F0.imprint","INTERSECT",VERTEX,{"derivedFrom":[subQ0,sQuery(id+"F0.wireOp",EDGE,"E14.3.0")]});Q70=makeQuery(id+"F0.imprint","IMPRINT",FACE,{"disambiguationData":[TD([[makeQuery(id+"F0.imprint","IMPRINT",EDGE,{"disambiguationData":[TD([[subQ1,1.0]])],"derivedFrom":subQ0}),1.0]])]});}
            var Q71;
            {var subQ0=sQuery(id+"F0.wireOp",EDGE,"E11");var subQ1=makeQuery(id+"F0.imprint","INTERSECT",VERTEX,{"derivedFrom":[subQ0,sQuery(id+"F0.wireOp",EDGE,"E14.3.1")]});Q71=makeQuery(id+"F0.imprint","IMPRINT",FACE,{"disambiguationData":[TD([[makeQuery(id+"F0.imprint","IMPRINT",EDGE,{"disambiguationData":[TD([[subQ1,-1.0]])],"derivedFrom":subQ0}),1.0]])]});}
            var Q72;
            {var subQ0=sQuery(id+"F0.wireOp",EDGE,"E14.3.1");Q72=makeQuery(id+"F0.imprint","IMPRINT",FACE,{"disambiguationData":[TD([[makeQuery(id+"F0.imprint","IMPRINT",EDGE,{"derivedFrom":subQ0}),1.0]])]});}
            var Q73;
            {var subQ0=sQuery(id+"F0.wireOp",EDGE,"E11");var subQ1=makeQuery(id+"F0.imprint","INTERSECT",VERTEX,{"derivedFrom":[subQ0,sQuery(id+"F0.wireOp",EDGE,"E14.4.0")]});Q73=makeQuery(id+"F0.imprint","IMPRINT",FACE,{"disambiguationData":[TD([[makeQuery(id+"F0.imprint","IMPRINT",EDGE,{"disambiguationData":[TD([[subQ1,1.0]])],"derivedFrom":subQ0}),1.0]])]});}
            var Q74;
            {var subQ0=sQuery(id+"F0.wireOp",EDGE,"E11");var subQ1=makeQuery(id+"F0.imprint","INTERSECT",VERTEX,{"derivedFrom":[subQ0,sQuery(id+"F0.wireOp",EDGE,"E14.4.1")]});Q74=makeQuery(id+"F0.imprint","IMPRINT",FACE,{"disambiguationData":[TD([[makeQuery(id+"F0.imprint","IMPRINT",EDGE,{"disambiguationData":[TD([[subQ1,-1.0]])],"derivedFrom":subQ0}),1.0]])]});}
            var Q75;
            {var subQ0=sQuery(id+"F0.wireOp",EDGE,"E14.4.1");Q75=makeQuery(id+"F0.imprint","IMPRINT",FACE,{"disambiguationData":[TD([[makeQuery(id+"F0.imprint","IMPRINT",EDGE,{"derivedFrom":subQ0}),1.0]])]});}
            var Q76;
            {var subQ0=sQuery(id+"F0.wireOp",EDGE,"E3");var subQ12=makeQuery(id+"F0.imprint","INTERSECT",VERTEX,{"derivedFrom":[subQ0,sQuery(id+"F0.wireOp",EDGE,"E5")]});Q76=makeQuery(id+"F0.imprint","IMPRINT",FACE,{"disambiguationData":[TD([[makeQuery(id+"F0.imprint","IMPRINT",EDGE,{"disambiguationData":[TD([[subQ12,1.0]])],"derivedFrom":subQ0}),-1.0]])]});}
            var Q77;
            {var subQ0=sQuery(id+"F0.wireOp",EDGE,"E3");var subQ13=makeQuery(id+"F0.imprint","INTERSECT",VERTEX,{"derivedFrom":[subQ0,sQuery(id+"F0.wireOp",EDGE,"E7.9.1")]});Q77=makeQuery(id+"F0.imprint","IMPRINT",FACE,{"disambiguationData":[TD([[makeQuery(id+"F0.imprint","IMPRINT",EDGE,{"disambiguationData":[TD([[subQ13,-1.0]])],"derivedFrom":subQ0}),-1.0]])]});}
            var Q78;
            {var subQ1=sQuery(id+"F0.wireOp",EDGE,"E1");var subQ6=sQuery(id+"F0.wireOp",EDGE,"E10.4.0");var subQ7=makeQuery(id+"F0.imprint","INTERSECT",VERTEX,{"derivedFrom":[subQ1,subQ6]});Q78=makeQuery(id+"F0.imprint","IMPRINT",FACE,{"disambiguationData":[TD([[makeQuery(id+"F0.imprint","IMPRINT",EDGE,{"disambiguationData":[TD([[subQ7,-1.0]])],"derivedFrom":subQ1}),-1.0]])]});}
            var Q79;
            {var subQ1=sQuery(id+"F0.wireOp",EDGE,"E1");var subQ6=sQuery(id+"F0.wireOp",EDGE,"E10.4.1");var subQ8=makeQuery(id+"F0.imprint","INTERSECT",VERTEX,{"derivedFrom":[subQ1,subQ6]});Q79=makeQuery(id+"F0.imprint","IMPRINT",FACE,{"disambiguationData":[TD([[makeQuery(id+"F0.imprint","IMPRINT",EDGE,{"disambiguationData":[TD([[subQ8,-1.0]])],"derivedFrom":subQ1}),-1.0]])]});}
            var Q80;
            {var subQ1=sQuery(id+"F0.wireOp",EDGE,"E1");var subQ5=sQuery(id+"F0.wireOp",EDGE,"E10.2.0");var subQ6=makeQuery(id+"F0.imprint","INTERSECT",VERTEX,{"derivedFrom":[subQ1,subQ5]});Q80=makeQuery(id+"F0.imprint","IMPRINT",FACE,{"disambiguationData":[TD([[makeQuery(id+"F0.imprint","IMPRINT",EDGE,{"disambiguationData":[TD([[subQ6,-1.0]])],"derivedFrom":subQ1}),-1.0]])]});}
            var Q81;
            {var subQ1=sQuery(id+"F0.wireOp",EDGE,"E1");var subQ6=sQuery(id+"F0.wireOp",EDGE,"E10.6.0");var subQ7=makeQuery(id+"F0.imprint","INTERSECT",VERTEX,{"derivedFrom":[subQ1,subQ6]});Q81=makeQuery(id+"F0.imprint","IMPRINT",FACE,{"disambiguationData":[TD([[makeQuery(id+"F0.imprint","IMPRINT",EDGE,{"disambiguationData":[TD([[subQ7,-1.0]])],"derivedFrom":subQ1}),-1.0]])]});}
            var Q82;
            {var subQ0=sQuery(id+"F0.wireOp",EDGE,"E10.7.1");var subQ1=sQuery(id+"F0.wireOp",EDGE,"E1");var subQ2=makeQuery(id+"F0.imprint","INTERSECT",VERTEX,{"derivedFrom":[subQ1,subQ0]});Q82=makeQuery(id+"F0.imprint","IMPRINT",FACE,{"disambiguationData":[TD([[makeQuery(id+"F0.imprint","IMPRINT",EDGE,{"disambiguationData":[TD([[subQ2,-1.0]])],"derivedFrom":subQ1}),-1.0]])]});}
            var Q83;
            {var subQ1=sQuery(id+"F0.wireOp",EDGE,"E1");var subQ6=sQuery(id+"F0.wireOp",EDGE,"E10.9.1");var subQ7=makeQuery(id+"F0.imprint","INTERSECT",VERTEX,{"derivedFrom":[subQ1,subQ6]});Q83=makeQuery(id+"F0.imprint","IMPRINT",FACE,{"disambiguationData":[TD([[makeQuery(id+"F0.imprint","IMPRINT",EDGE,{"disambiguationData":[TD([[subQ7,1.0]])],"derivedFrom":subQ1}),-1.0]])]});}
            var Q84;
            {var subQ1=sQuery(id+"F0.wireOp",EDGE,"E1");var subQ7=sQuery(id+"F0.wireOp",EDGE,"E10.9.1");var subQ8=makeQuery(id+"F0.imprint","INTERSECT",VERTEX,{"derivedFrom":[subQ1,subQ7]});Q84=makeQuery(id+"F0.imprint","IMPRINT",FACE,{"disambiguationData":[TD([[makeQuery(id+"F0.imprint","IMPRINT",EDGE,{"disambiguationData":[TD([[subQ8,-1.0]])],"derivedFrom":subQ1}),-1.0]])]});}
            var Q85;
            {var subQ1=sQuery(id+"F0.wireOp",EDGE,"E1");var subQ5=makeQuery(id+"F0.imprint","INTERSECT",VERTEX,{"derivedFrom":[subQ1,sQuery(id+"F0.wireOp",EDGE,"E16.MirrorCS")]});Q85=makeQuery(id+"F0.imprint","IMPRINT",FACE,{"disambiguationData":[TD([[makeQuery(id+"F0.imprint","IMPRINT",EDGE,{"disambiguationData":[TD([[subQ5,-1.0]])],"derivedFrom":subQ1}),-1.0]])]});}
            var Q86;
            {var subQ1=sQuery(id+"F0.wireOp",EDGE,"E1");var subQ5=makeQuery(id+"F0.imprint","INTERSECT",VERTEX,{"derivedFrom":[subQ1,sQuery(id+"F0.wireOp",EDGE,"E15")]});Q86=makeQuery(id+"F0.imprint","IMPRINT",FACE,{"disambiguationData":[TD([[makeQuery(id+"F0.imprint","IMPRINT",EDGE,{"disambiguationData":[TD([[subQ5,1.0]])],"derivedFrom":subQ1}),-1.0]])]});}
            var Q87;
            {var subQ1=sQuery(id+"F0.wireOp",EDGE,"E1");var subQ5=sQuery(id+"F0.wireOp",EDGE,"E10.1.0");var subQ6=makeQuery(id+"F0.imprint","INTERSECT",VERTEX,{"derivedFrom":[subQ1,subQ5]});Q87=makeQuery(id+"F0.imprint","IMPRINT",FACE,{"disambiguationData":[TD([[makeQuery(id+"F0.imprint","IMPRINT",EDGE,{"disambiguationData":[TD([[subQ6,-1.0]])],"derivedFrom":subQ1}),-1.0]])]});}
            var Q88;
            {var subQ1=sQuery(id+"F0.wireOp",EDGE,"E1");var subQ7=sQuery(id+"F0.wireOp",EDGE,"E10.2.1");var subQ8=makeQuery(id+"F0.imprint","INTERSECT",VERTEX,{"derivedFrom":[subQ1,subQ7]});Q88=makeQuery(id+"F0.imprint","IMPRINT",FACE,{"disambiguationData":[TD([[makeQuery(id+"F0.imprint","IMPRINT",EDGE,{"disambiguationData":[TD([[subQ8,-1.0]])],"derivedFrom":subQ1}),-1.0]])]});}
            var Q89;
            {var subQ1=sQuery(id+"F0.wireOp",EDGE,"E1");var subQ5=sQuery(id+"F0.wireOp",EDGE,"E10.9.0");var subQ6=makeQuery(id+"F0.imprint","INTERSECT",VERTEX,{"derivedFrom":[subQ1,subQ5]});Q89=makeQuery(id+"F0.imprint","IMPRINT",FACE,{"disambiguationData":[TD([[makeQuery(id+"F0.imprint","IMPRINT",EDGE,{"disambiguationData":[TD([[subQ6,-1.0]])],"derivedFrom":subQ1}),-1.0]])]});}
            var Q90;
            {var subQ0=sQuery(id+"F0.wireOp",EDGE,"E22");var subQ1=sQuery(id+"F0.wireOp",EDGE,"E10.9.0");var subQ2=makeQuery(id+"F0.imprint","INTERSECT",VERTEX,{"derivedFrom":[subQ1,subQ0]});Q90=makeQuery(id+"F0.imprint","IMPRINT",FACE,{"disambiguationData":[TD([[makeQuery(id+"F0.imprint","IMPRINT",EDGE,{"disambiguationData":[TD([[subQ2,-1.0]])],"derivedFrom":subQ1}),1.0]])]});}
            var Q91;
            {var subQ0=sQuery(id+"F0.wireOp",EDGE,"E22");var subQ1=sQuery(id+"F0.wireOp",EDGE,"E10.8.0");var subQ2=makeQuery(id+"F0.imprint","INTERSECT",VERTEX,{"derivedFrom":[subQ1,subQ0]});Q91=makeQuery(id+"F0.imprint","IMPRINT",FACE,{"disambiguationData":[TD([[makeQuery(id+"F0.imprint","IMPRINT",EDGE,{"disambiguationData":[TD([[subQ2,-1.0]])],"derivedFrom":subQ1}),1.0]])]});}
            var Q92;
            {var subQ0=sQuery(id+"F0.wireOp",EDGE,"E22");var subQ1=sQuery(id+"F0.wireOp",EDGE,"E10.10.0");var subQ2=makeQuery(id+"F0.imprint","INTERSECT",VERTEX,{"derivedFrom":[subQ1,subQ0]});Q92=makeQuery(id+"F0.imprint","IMPRINT",FACE,{"disambiguationData":[TD([[makeQuery(id+"F0.imprint","IMPRINT",EDGE,{"disambiguationData":[TD([[subQ2,-1.0]])],"derivedFrom":subQ1}),1.0]])]});}
            var Q93;
            {var subQ0=sQuery(id+"F0.wireOp",EDGE,"E22");var subQ1=sQuery(id+"F0.wireOp",EDGE,"E10.11.0");var subQ2=makeQuery(id+"F0.imprint","INTERSECT",VERTEX,{"derivedFrom":[subQ1,subQ0]});Q93=makeQuery(id+"F0.imprint","IMPRINT",FACE,{"disambiguationData":[TD([[makeQuery(id+"F0.imprint","IMPRINT",EDGE,{"disambiguationData":[TD([[subQ2,-1.0]])],"derivedFrom":subQ1}),1.0]])]});}
            var Q94;
            {var subQ0=sQuery(id+"F0.wireOp",EDGE,"E22");var subQ1=sQuery(id+"F0.wireOp",EDGE,"E10.7.0");var subQ2=makeQuery(id+"F0.imprint","INTERSECT",VERTEX,{"derivedFrom":[subQ1,subQ0]});Q94=makeQuery(id+"F0.imprint","IMPRINT",FACE,{"disambiguationData":[TD([[makeQuery(id+"F0.imprint","IMPRINT",EDGE,{"disambiguationData":[TD([[subQ2,-1.0]])],"derivedFrom":subQ1}),1.0]])]});}
            var Q95;
            {var subQ0=sQuery(id+"F0.wireOp",EDGE,"E22");var subQ1=sQuery(id+"F0.wireOp",EDGE,"E10.6.0");var subQ2=makeQuery(id+"F0.imprint","INTERSECT",VERTEX,{"derivedFrom":[subQ1,subQ0]});Q95=makeQuery(id+"F0.imprint","IMPRINT",FACE,{"disambiguationData":[TD([[makeQuery(id+"F0.imprint","IMPRINT",EDGE,{"disambiguationData":[TD([[subQ2,-1.0]])],"derivedFrom":subQ1}),1.0]])]});}
            var Q96;
            {var subQ0=sQuery(id+"F0.wireOp",EDGE,"E22");var subQ1=sQuery(id+"F0.wireOp",EDGE,"E10.5.0");var subQ2=makeQuery(id+"F0.imprint","INTERSECT",VERTEX,{"derivedFrom":[subQ1,subQ0]});Q96=makeQuery(id+"F0.imprint","IMPRINT",FACE,{"disambiguationData":[TD([[makeQuery(id+"F0.imprint","IMPRINT",EDGE,{"disambiguationData":[TD([[subQ2,-1.0]])],"derivedFrom":subQ1}),1.0]])]});}
            var Q97;
            {var subQ0=sQuery(id+"F0.wireOp",EDGE,"E22");var subQ1=sQuery(id+"F0.wireOp",EDGE,"E10.4.0");var subQ2=makeQuery(id+"F0.imprint","INTERSECT",VERTEX,{"derivedFrom":[subQ1,subQ0]});Q97=makeQuery(id+"F0.imprint","IMPRINT",FACE,{"disambiguationData":[TD([[makeQuery(id+"F0.imprint","IMPRINT",EDGE,{"disambiguationData":[TD([[subQ2,-1.0]])],"derivedFrom":subQ1}),1.0]])]});}
            var Q98;
            {var subQ0=sQuery(id+"F0.wireOp",EDGE,"E22");var subQ1=sQuery(id+"F0.wireOp",EDGE,"E10.3.0");var subQ2=makeQuery(id+"F0.imprint","INTERSECT",VERTEX,{"derivedFrom":[subQ1,subQ0]});Q98=makeQuery(id+"F0.imprint","IMPRINT",FACE,{"disambiguationData":[TD([[makeQuery(id+"F0.imprint","IMPRINT",EDGE,{"disambiguationData":[TD([[subQ2,-1.0]])],"derivedFrom":subQ1}),1.0]])]});}
            var Q99;
            {var subQ0=sQuery(id+"F0.wireOp",EDGE,"E22");var subQ1=sQuery(id+"F0.wireOp",EDGE,"E10.2.0");var subQ2=makeQuery(id+"F0.imprint","INTERSECT",VERTEX,{"derivedFrom":[subQ1,subQ0]});Q99=makeQuery(id+"F0.imprint","IMPRINT",FACE,{"disambiguationData":[TD([[makeQuery(id+"F0.imprint","IMPRINT",EDGE,{"disambiguationData":[TD([[subQ2,-1.0]])],"derivedFrom":subQ1}),1.0]])]});}
            var Q100;
            {var subQ0=sQuery(id+"F0.wireOp",EDGE,"E22");var subQ1=sQuery(id+"F0.wireOp",EDGE,"E10.1.0");var subQ2=makeQuery(id+"F0.imprint","INTERSECT",VERTEX,{"derivedFrom":[subQ1,subQ0]});Q100=makeQuery(id+"F0.imprint","IMPRINT",FACE,{"disambiguationData":[TD([[makeQuery(id+"F0.imprint","IMPRINT",EDGE,{"disambiguationData":[TD([[subQ2,-1.0]])],"derivedFrom":subQ1}),1.0]])]});}
            var Q101;
            {var subQ0=sQuery(id+"F0.wireOp",EDGE,"E22");var subQ1=sQuery(id+"F0.wireOp",EDGE,"E8");var subQ2=makeQuery(id+"F0.imprint","INTERSECT",VERTEX,{"derivedFrom":[subQ1,subQ0]});Q101=makeQuery(id+"F0.imprint","IMPRINT",FACE,{"disambiguationData":[TD([[makeQuery(id+"F0.imprint","IMPRINT",EDGE,{"disambiguationData":[TD([[subQ2,-1.0]])],"derivedFrom":subQ1}),-1.0]])]});}
            var Q102;
            {var subQ0=sQuery(id+"F0.wireOp",EDGE,"E26.1.0");Q102=makeQuery(id+"F0.imprint","IMPRINT",FACE,{"disambiguationData":[TD([[makeQuery(id+"F0.imprint","IMPRINT",EDGE,{"derivedFrom":subQ0}),1.0]])]});}
            var Q103;
            {var subQ5=sQuery(id+"F0.wireOp",EDGE,"E25");Q103=makeQuery(id+"F0.imprint","IMPRINT",FACE,{"disambiguationData":[TD([[makeQuery(id+"F0.imprint","IMPRINT",EDGE,{"derivedFrom":subQ5}),1.0]])]});}
            var Q104;
            {var subQ5=sQuery(id+"F0.wireOp",EDGE,"E24");Q104=makeQuery(id+"F0.imprint","IMPRINT",FACE,{"disambiguationData":[TD([[makeQuery(id+"F0.imprint","IMPRINT",EDGE,{"derivedFrom":subQ5}),-1.0]])]});}
            var Q105;
            {var subQ0=sQuery(id+"F0.wireOp",EDGE,"E26.11.0");Q105=makeQuery(id+"F0.imprint","IMPRINT",FACE,{"disambiguationData":[TD([[makeQuery(id+"F0.imprint","IMPRINT",EDGE,{"derivedFrom":subQ0}),1.0]])]});}
            var Q106;
            {var subQ0=sQuery(id+"F0.wireOp",EDGE,"E26.10.0");Q106=makeQuery(id+"F0.imprint","IMPRINT",FACE,{"disambiguationData":[TD([[makeQuery(id+"F0.imprint","IMPRINT",EDGE,{"derivedFrom":subQ0}),1.0]])]});}
            var Q107;
            {var subQ0=sQuery(id+"F0.wireOp",EDGE,"E26.9.0");Q107=makeQuery(id+"F0.imprint","IMPRINT",FACE,{"disambiguationData":[TD([[makeQuery(id+"F0.imprint","IMPRINT",EDGE,{"derivedFrom":subQ0}),1.0]])]});}
            var Q108;
            {var subQ0=sQuery(id+"F0.wireOp",EDGE,"E26.8.0");Q108=makeQuery(id+"F0.imprint","IMPRINT",FACE,{"disambiguationData":[TD([[makeQuery(id+"F0.imprint","IMPRINT",EDGE,{"derivedFrom":subQ0}),1.0]])]});}
            var Q109;
            {var subQ0=sQuery(id+"F0.wireOp",EDGE,"E26.7.0");Q109=makeQuery(id+"F0.imprint","IMPRINT",FACE,{"disambiguationData":[TD([[makeQuery(id+"F0.imprint","IMPRINT",EDGE,{"derivedFrom":subQ0}),1.0]])]});}
            var Q110;
            {var subQ5=sQuery(id+"F0.wireOp",EDGE,"E26.6.0");Q110=makeQuery(id+"F0.imprint","IMPRINT",FACE,{"disambiguationData":[TD([[makeQuery(id+"F0.imprint","IMPRINT",EDGE,{"derivedFrom":subQ5}),1.0]])]});}
            var Q111;
            {var subQ5=sQuery(id+"F0.wireOp",EDGE,"E26.6.1");Q111=makeQuery(id+"F0.imprint","IMPRINT",FACE,{"disambiguationData":[TD([[makeQuery(id+"F0.imprint","IMPRINT",EDGE,{"derivedFrom":subQ5}),-1.0]])]});}
            var Q112;
            {var subQ0=sQuery(id+"F0.wireOp",EDGE,"E26.5.0");Q112=makeQuery(id+"F0.imprint","IMPRINT",FACE,{"disambiguationData":[TD([[makeQuery(id+"F0.imprint","IMPRINT",EDGE,{"derivedFrom":subQ0}),1.0]])]});}
            var Q113;
            {var subQ0=sQuery(id+"F0.wireOp",EDGE,"E26.4.0");Q113=makeQuery(id+"F0.imprint","IMPRINT",FACE,{"disambiguationData":[TD([[makeQuery(id+"F0.imprint","IMPRINT",EDGE,{"derivedFrom":subQ0}),1.0]])]});}
            var Q114;
            {var subQ0=sQuery(id+"F0.wireOp",EDGE,"E26.3.0");Q114=makeQuery(id+"F0.imprint","IMPRINT",FACE,{"disambiguationData":[TD([[makeQuery(id+"F0.imprint","IMPRINT",EDGE,{"derivedFrom":subQ0}),1.0]])]});}
            var Q115;
            {var subQ0=sQuery(id+"F0.wireOp",EDGE,"E26.2.0");Q115=makeQuery(id+"F0.imprint","IMPRINT",FACE,{"disambiguationData":[TD([[makeQuery(id+"F0.imprint","IMPRINT",EDGE,{"derivedFrom":subQ0}),1.0]])]});}
            extrude(context, id + "F1", {"entities" : qUnion([Q0, Q1, Q2, Q3, Q4, Q5, Q6, Q7, Q8, Q9, Q10, Q11, Q12, Q13, Q14, Q15, Q16, Q17, Q18, Q19, Q20, Q21, Q22, Q23, Q24, Q25, Q26, Q27, Q28, Q29, Q30, Q31, Q32, Q33, Q34, Q35, Q36, Q37, Q38, Q39, Q40, Q41, Q42, Q43, Q44, Q45, Q46, Q47, Q48, Q49, Q50, Q51, Q52, Q53, Q54, Q55, Q56, Q57, Q58, Q59, Q60, Q61, Q62, Q63, Q64, Q65, Q66, Q67, Q68, Q69, Q70, Q71, Q72, Q73, Q74, Q75, Q76, Q77, Q78, Q79, Q80, Q81, Q82, Q83, Q84, Q85, Q86, Q87, Q88, Q89, Q90, Q91, Q92, Q93, Q94, Q95, Q96, Q97, Q98, Q99, Q100, Q101, Q102, Q103, Q104, Q105, Q106, Q107, Q108, Q109, Q110, Q111, Q112, Q113, Q114, Q115]), "depth" : 5.08 * mm, "offsetDistance" : 25 * mm});
        }
    });
